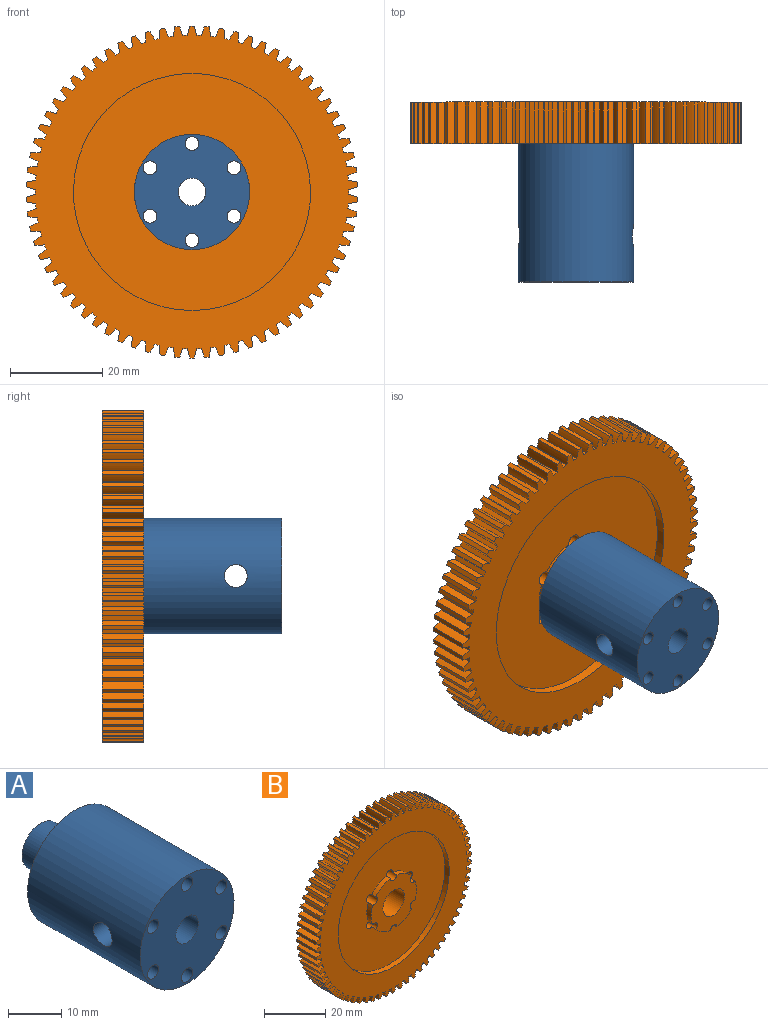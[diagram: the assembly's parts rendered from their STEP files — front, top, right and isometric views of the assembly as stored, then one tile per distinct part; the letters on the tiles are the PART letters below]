
ASSEMBLY  parts=2 mates=1
PART A: 14 faces, bbox 25x39x25 mm
  f0: cylinder r=3mm len=39mm, axis (0,1,0), area 691mm2, adj f2,f10,f11,f13
  f1: cylinder r=12.5mm len=30mm, axis (0,1,0), area 2316.8mm2, adj f2,f3,f10,f11
  f2: plane 25x25mm, normal (0,-1,0), area 420.2mm2, adj f0,f1,f4,f5,f6,f7,f8,f9
  f3: plane 25x25mm, normal (0,1,0), area 369.9mm2, adj f1,f4,f5,f6,f7,f8,f9,f12
  f4: cylinder r=1.5mm len=30mm, axis (0,1,0), area 282.7mm2, adj f2,f3
  f5: cylinder r=1.5mm len=30mm, axis (0,1,0), area 282.7mm2, adj f2,f3
  f6: cylinder r=1.5mm len=30mm, axis (0,1,0), area 282.7mm2, adj f2,f3
  f7: cylinder r=1.5mm len=30mm, axis (0,1,0), area 282.7mm2, adj f2,f3
  f8: cylinder r=1.5mm len=30mm, axis (0,1,0), area 282.7mm2, adj f2,f3
  f9: cylinder r=1.5mm len=30mm, axis (0,1,0), area 282.7mm2, adj f2,f3
  f10: cylinder r=2.5mm len=10.84mm, axis (-1,0,0), area 157mm2, adj f0,f1
  f11: cylinder r=2.5mm len=10.84mm, axis (-1,0,0), area 157mm2, adj f0,f1
  f12: cylinder r=5mm len=10mm, axis (0,-1,0), area 282.7mm2, adj f3,f13
  f13: plane 10x10mm, normal (0,1,0), area 50.3mm2, adj f0,f12
PART B: 307 faces, bbox 72x9x72 mm
  f0: cylinder r=10.5mm len=6.76mm, axis (0,1,0), area 16mm2, adj f296,f298,f305,f306
  f1: cylinder r=10.5mm len=6.76mm, axis (0,1,0), area 16mm2, adj f296,f298,f301,f306
  f2: cylinder r=10.5mm len=7.8mm, axis (0,1,0), area 16mm2, adj f296,f298,f304,f305
  f3: cylinder r=10.5mm len=6.76mm, axis (0,1,0), area 16mm2, adj f296,f298,f303,f304
  f4: cylinder r=10.5mm len=6.76mm, axis (0,1,0), area 16mm2, adj f296,f298,f302,f303
  f5: cylinder r=10.5mm len=7.8mm, axis (0,1,0), area 16mm2, adj f296,f298,f301,f302
  f6: cylinder r=10.5mm len=6.76mm, axis (0,1,0), area 16mm2, adj f12,f300,f305,f306
  f7: cylinder r=10.5mm len=6.76mm, axis (0,1,0), area 16mm2, adj f12,f300,f301,f306
  f8: cylinder r=10.5mm len=7.8mm, axis (0,1,0), area 16mm2, adj f12,f300,f304,f305
  f9: cylinder r=10.5mm len=6.76mm, axis (0,1,0), area 16mm2, adj f12,f300,f303,f304
  f10: cylinder r=10.5mm len=6.76mm, axis (0,1,0), area 16mm2, adj f12,f300,f302,f303
  f11: cylinder r=10.5mm len=7.8mm, axis (0,1,0), area 16mm2, adj f12,f300,f301,f302
  f12: plane 21x20.79mm, normal (0,1,0), area 247.3mm2, adj f6,f7,f8,f9,f10,f11,f297,f301
  f13: cylinder r=34mm len=9mm, axis (0,1,0), area 9.8mm2, adj f82,f87,f88,f193
  f14: cylinder r=34mm len=9mm, axis (0,1,0), area 9.8mm2, adj f87,f88,f190,f192
  f15: cylinder r=34mm len=9mm, axis (0,1,0), area 9.8mm2, adj f87,f88,f187,f189
  f16: cylinder r=34mm len=9mm, axis (0,1,0), area 9.8mm2, adj f87,f88,f184,f186
  f17: cylinder r=34mm len=9mm, axis (0,1,0), area 9.8mm2, adj f87,f88,f181,f183
  f18: cylinder r=34mm len=9mm, axis (0,1,0), area 9.8mm2, adj f87,f88,f178,f180
  f19: cylinder r=34mm len=9mm, axis (0,1,0), area 9.8mm2, adj f87,f88,f175,f177
  f20: cylinder r=34mm len=9mm, axis (0,1,0), area 9.8mm2, adj f87,f88,f172,f174
  f21: cylinder r=34mm len=9mm, axis (0,1,0), area 9.8mm2, adj f87,f88,f169,f171
  f22: cylinder r=34mm len=9mm, axis (0,1,0), area 9.8mm2, adj f87,f88,f166,f168
  f23: cylinder r=34mm len=9mm, axis (0,1,0), area 9.8mm2, adj f87,f88,f163,f165
  f24: cylinder r=34mm len=9mm, axis (0,1,0), area 9.8mm2, adj f87,f88,f160,f162
  f25: cylinder r=34mm len=9mm, axis (0,1,0), area 9.8mm2, adj f87,f88,f157,f159
  f26: cylinder r=34mm len=9mm, axis (0,1,0), area 9.8mm2, adj f87,f88,f154,f156
  f27: cylinder r=34mm len=9mm, axis (0,1,0), area 9.8mm2, adj f87,f88,f151,f153
  f28: cylinder r=34mm len=9mm, axis (0,1,0), area 9.8mm2, adj f87,f88,f148,f150
  f29: cylinder r=34mm len=9mm, axis (0,1,0), area 9.8mm2, adj f87,f88,f145,f147
  f30: cylinder r=34mm len=9mm, axis (0,1,0), area 9.8mm2, adj f87,f88,f142,f144
  f31: cylinder r=34mm len=9mm, axis (0,1,0), area 9.8mm2, adj f87,f88,f139,f141
  f32: cylinder r=34mm len=9mm, axis (0,1,0), area 9.8mm2, adj f87,f88,f136,f138
  f33: cylinder r=34mm len=9mm, axis (0,1,0), area 9.8mm2, adj f87,f88,f133,f135
  f34: cylinder r=34mm len=9mm, axis (0,1,0), area 9.8mm2, adj f87,f88,f130,f132
  f35: cylinder r=34mm len=9mm, axis (0,1,0), area 9.8mm2, adj f87,f88,f127,f129
  f36: cylinder r=34mm len=9mm, axis (0,1,0), area 9.8mm2, adj f87,f88,f124,f126
  f37: cylinder r=34mm len=9mm, axis (0,1,0), area 9.8mm2, adj f87,f88,f121,f123
  f38: cylinder r=34mm len=9mm, axis (0,1,0), area 9.8mm2, adj f87,f88,f118,f120
  f39: cylinder r=34mm len=9mm, axis (0,1,0), area 9.8mm2, adj f87,f88,f115,f117
  f40: cylinder r=34mm len=9mm, axis (0,1,0), area 9.8mm2, adj f87,f88,f112,f114
  f41: cylinder r=34mm len=9mm, axis (0,1,0), area 9.8mm2, adj f87,f88,f109,f111
  f42: cylinder r=34mm len=9mm, axis (0,1,0), area 9.8mm2, adj f87,f88,f106,f108
  f43: cylinder r=34mm len=9mm, axis (0,1,0), area 9.8mm2, adj f87,f88,f103,f105
  f44: cylinder r=34mm len=9mm, axis (0,1,0), area 9.8mm2, adj f87,f88,f100,f102
  f45: cylinder r=34mm len=9mm, axis (0,1,0), area 9.8mm2, adj f87,f88,f97,f99
  f46: cylinder r=34mm len=9mm, axis (0,1,0), area 9.8mm2, adj f87,f88,f94,f96
  f47: cylinder r=34mm len=9mm, axis (0,1,0), area 9.8mm2, adj f87,f88,f91,f93
  f48: cylinder r=34mm len=9mm, axis (0,1,0), area 9.8mm2, adj f87,f88,f90,f294
  f49: cylinder r=34mm len=9mm, axis (0,1,0), area 9.8mm2, adj f87,f88,f292,f293
  f50: cylinder r=34mm len=9mm, axis (0,1,0), area 9.8mm2, adj f87,f88,f289,f291
  f51: cylinder r=34mm len=9mm, axis (0,1,0), area 9.8mm2, adj f87,f88,f286,f288
  f52: cylinder r=34mm len=9mm, axis (0,1,0), area 9.8mm2, adj f87,f88,f283,f285
  f53: cylinder r=34mm len=9mm, axis (0,1,0), area 9.8mm2, adj f87,f88,f280,f282
  f54: cylinder r=34mm len=9mm, axis (0,1,0), area 9.8mm2, adj f87,f88,f277,f279
  f55: cylinder r=34mm len=9mm, axis (0,1,0), area 9.8mm2, adj f87,f88,f274,f276
  f56: cylinder r=34mm len=9mm, axis (0,1,0), area 9.8mm2, adj f87,f88,f271,f273
  f57: cylinder r=34mm len=9mm, axis (0,1,0), area 9.8mm2, adj f87,f88,f268,f270
  f58: cylinder r=34mm len=9mm, axis (0,1,0), area 9.8mm2, adj f87,f88,f265,f267
  f59: cylinder r=34mm len=9mm, axis (0,1,0), area 9.8mm2, adj f87,f88,f262,f264
  f60: cylinder r=34mm len=9mm, axis (0,1,0), area 9.8mm2, adj f87,f88,f259,f261
  f61: cylinder r=34mm len=9mm, axis (0,1,0), area 9.8mm2, adj f87,f88,f256,f258
  f62: cylinder r=34mm len=9mm, axis (0,1,0), area 9.8mm2, adj f87,f88,f253,f255
  f63: cylinder r=34mm len=9mm, axis (0,1,0), area 9.8mm2, adj f87,f88,f250,f252
  f64: cylinder r=34mm len=9mm, axis (0,1,0), area 9.8mm2, adj f87,f88,f247,f249
  f65: cylinder r=34mm len=9mm, axis (0,1,0), area 9.8mm2, adj f87,f88,f244,f246
  f66: cylinder r=34mm len=9mm, axis (0,1,0), area 9.8mm2, adj f87,f88,f241,f243
  f67: cylinder r=34mm len=9mm, axis (0,1,0), area 9.8mm2, adj f87,f88,f238,f240
  f68: cylinder r=34mm len=9mm, axis (0,1,0), area 9.8mm2, adj f87,f88,f235,f237
  f69: cylinder r=34mm len=9mm, axis (0,1,0), area 9.8mm2, adj f87,f88,f232,f234
  f70: cylinder r=34mm len=9mm, axis (0,1,0), area 9.8mm2, adj f87,f88,f229,f231
  f71: cylinder r=34mm len=9mm, axis (0,1,0), area 9.8mm2, adj f87,f88,f226,f228
  f72: cylinder r=34mm len=9mm, axis (0,1,0), area 9.8mm2, adj f87,f88,f223,f225
  f73: cylinder r=34mm len=9mm, axis (0,1,0), area 9.8mm2, adj f87,f88,f220,f222
  f74: cylinder r=34mm len=9mm, axis (0,1,0), area 9.8mm2, adj f87,f88,f217,f219
  f75: cylinder r=34mm len=9mm, axis (0,1,0), area 9.8mm2, adj f87,f88,f214,f216
  f76: cylinder r=34mm len=9mm, axis (0,1,0), area 9.8mm2, adj f87,f88,f211,f213
  f77: cylinder r=34mm len=9mm, axis (0,1,0), area 9.8mm2, adj f87,f88,f208,f210
  f78: cylinder r=34mm len=9mm, axis (0,1,0), area 9.8mm2, adj f87,f88,f205,f207
  f79: cylinder r=34mm len=9mm, axis (0,1,0), area 9.8mm2, adj f87,f88,f202,f204
  f80: cylinder r=34mm len=9mm, axis (0,1,0), area 9.8mm2, adj f87,f88,f199,f201
  f81: cylinder r=34mm len=9mm, axis (0,1,0), area 9.8mm2, adj f87,f88,f195,f198
  f82: cylinder r=11.84mm len=9mm, axis (0,1,0), area 18.7mm2, adj f13,f85,f87,f88
  f83: cylinder r=34mm len=9mm, axis (0,1,0), area 9.8mm2, adj f84,f87,f88,f196
  f84: cylinder r=11.84mm len=9mm, axis (0,1,0), area 18.7mm2, adj f83,f85,f87,f88
  f85: plane 9x1mm, normal (0,0,1), area 9mm2, adj f82,f84,f87,f88
  f86: cylinder r=25.7mm len=51.4mm, axis (0,1,0), area 323mm2, adj f87,f296
  f87: plane 72x71.97mm, normal (0,-1,0), area 1772.8mm2, adj f13,f14,f15,f16,f17,f18,f19,f20
  f88: plane 72x71.97mm, normal (0,1,0), area 1772.8mm2, adj f13,f14,f15,f16,f17,f18,f19,f20
  f89: plane 9x1mm, normal (0,0,-1), area 9mm2, adj f87,f88,f90,f91
  f90: cylinder r=11.84mm len=9mm, axis (0,1,0), area 18.7mm2, adj f48,f87,f88,f89
  f91: cylinder r=11.84mm len=9mm, axis (0,1,0), area 18.7mm2, adj f47,f87,f88,f89
  f92: plane 9x1mm, normal (-0.09,0,-1), area 9mm2, adj f87,f88,f93,f94
  f93: cylinder r=11.84mm len=9mm, axis (0,1,0), area 18.7mm2, adj f47,f87,f88,f92
  f94: cylinder r=11.84mm len=9mm, axis (0,1,0), area 18.7mm2, adj f46,f87,f88,f92
  f95: plane 9x0.98mm, normal (-0.18,0,-0.98), area 9mm2, adj f87,f88,f96,f97
  f96: cylinder r=11.84mm len=9mm, axis (0,1,0), area 18.7mm2, adj f46,f87,f88,f95
  f97: cylinder r=11.84mm len=9mm, axis (0,1,0), area 18.7mm2, adj f45,f87,f88,f95
  f98: plane 9x0.96mm, normal (-0.27,0,-0.96), area 9mm2, adj f87,f88,f99,f100
  f99: cylinder r=11.84mm len=9mm, axis (0,1,0), area 18.7mm2, adj f45,f87,f88,f98
  f100: cylinder r=11.84mm len=9mm, axis (0,1,0), area 18.7mm2, adj f44,f87,f88,f98
  f101: plane 9x0.94mm, normal (-0.35,0,-0.94), area 9mm2, adj f87,f88,f102,f103
  f102: cylinder r=11.84mm len=9mm, axis (0,1,0), area 18.7mm2, adj f44,f87,f88,f101
  f103: cylinder r=11.84mm len=9mm, axis (0,1,0), area 18.7mm2, adj f43,f87,f88,f101
  f104: plane 9x0.9mm, normal (-0.43,0,-0.9), area 9mm2, adj f87,f88,f105,f106
  f105: cylinder r=11.84mm len=9mm, axis (0,1,0), area 18.7mm2, adj f43,f87,f88,f104
  f106: cylinder r=11.84mm len=9mm, axis (0,1,0), area 18.7mm2, adj f42,f87,f88,f104
  f107: plane 9x0.86mm, normal (-0.51,0,-0.86), area 9mm2, adj f87,f88,f108,f109
  f108: cylinder r=11.84mm len=9mm, axis (0,1,0), area 18.7mm2, adj f42,f87,f88,f107
  f109: cylinder r=11.84mm len=9mm, axis (0,1,0), area 18.7mm2, adj f41,f87,f88,f107
  f110: plane 9x0.81mm, normal (-0.59,0,-0.81), area 9mm2, adj f87,f88,f111,f112
  f111: cylinder r=11.84mm len=9mm, axis (0,1,0), area 18.7mm2, adj f41,f87,f88,f110
  f112: cylinder r=11.84mm len=9mm, axis (0,1,0), area 18.7mm2, adj f40,f87,f88,f110
  f113: plane 9x0.75mm, normal (-0.66,0,-0.75), area 9mm2, adj f87,f88,f114,f115
  f114: cylinder r=11.84mm len=9mm, axis (0,1,0), area 18.7mm2, adj f40,f87,f88,f113
  f115: cylinder r=11.84mm len=9mm, axis (0,1,0), area 18.7mm2, adj f39,f87,f88,f113
  f116: plane 9x0.72mm, normal (-0.72,0,-0.69), area 9mm2, adj f87,f88,f117,f118
  f117: cylinder r=11.84mm len=9mm, axis (0,1,0), area 18.7mm2, adj f39,f87,f88,f116
  f118: cylinder r=11.84mm len=9mm, axis (0,1,0), area 18.7mm2, adj f38,f87,f88,f116
  f119: plane 9x0.78mm, normal (-0.78,0,-0.62), area 9mm2, adj f87,f88,f120,f121
  f120: cylinder r=11.84mm len=9mm, axis (0,1,0), area 18.7mm2, adj f38,f87,f88,f119
  f121: cylinder r=11.84mm len=9mm, axis (0,1,0), area 18.7mm2, adj f37,f87,f88,f119
  f122: plane 9x0.83mm, normal (-0.83,0,-0.55), area 9mm2, adj f87,f88,f123,f124
  f123: cylinder r=11.84mm len=9mm, axis (0,1,0), area 18.7mm2, adj f37,f87,f88,f122
  f124: cylinder r=11.84mm len=9mm, axis (0,1,0), area 18.7mm2, adj f36,f87,f88,f122
  f125: plane 9x0.88mm, normal (-0.88,0,-0.47), area 9mm2, adj f87,f88,f126,f127
  f126: cylinder r=11.84mm len=9mm, axis (0,1,0), area 18.7mm2, adj f36,f87,f88,f125
  f127: cylinder r=11.84mm len=9mm, axis (0,1,0), area 18.7mm2, adj f35,f87,f88,f125
  f128: plane 9x0.92mm, normal (-0.92,0,-0.39), area 9mm2, adj f87,f88,f129,f130
  f129: cylinder r=11.84mm len=9mm, axis (0,1,0), area 18.7mm2, adj f35,f87,f88,f128
  f130: cylinder r=11.84mm len=9mm, axis (0,1,0), area 18.7mm2, adj f34,f87,f88,f128
  f131: plane 9x0.95mm, normal (-0.95,0,-0.31), area 9mm2, adj f87,f88,f132,f133
  f132: cylinder r=11.84mm len=9mm, axis (0,1,0), area 18.7mm2, adj f34,f87,f88,f131
  f133: cylinder r=11.84mm len=9mm, axis (0,1,0), area 18.7mm2, adj f33,f87,f88,f131
  f134: plane 9x0.98mm, normal (-0.97,0,-0.22), area 9mm2, adj f87,f88,f135,f136
  f135: cylinder r=11.84mm len=9mm, axis (0,1,0), area 18.7mm2, adj f33,f87,f88,f134
  f136: cylinder r=11.84mm len=9mm, axis (0,1,0), area 18.7mm2, adj f32,f87,f88,f134
  f137: plane 9x0.99mm, normal (-0.99,0,-0.13), area 9mm2, adj f87,f88,f138,f139
  f138: cylinder r=11.84mm len=9mm, axis (0,1,0), area 18.7mm2, adj f32,f87,f88,f137
  f139: cylinder r=11.84mm len=9mm, axis (0,1,0), area 18.7mm2, adj f31,f87,f88,f137
  f140: plane 9x1mm, normal (-1,0,-0.04), area 9mm2, adj f87,f88,f141,f142
  f141: cylinder r=11.84mm len=9mm, axis (0,1,0), area 18.7mm2, adj f31,f87,f88,f140
  f142: cylinder r=11.84mm len=9mm, axis (0,1,0), area 18.7mm2, adj f30,f87,f88,f140
  f143: plane 9x1mm, normal (-1,0,0.04), area 9mm2, adj f87,f88,f144,f145
  f144: cylinder r=11.84mm len=9mm, axis (0,1,0), area 18.7mm2, adj f30,f87,f88,f143
  f145: cylinder r=11.84mm len=9mm, axis (0,1,0), area 18.7mm2, adj f29,f87,f88,f143
  f146: plane 9x0.99mm, normal (-0.99,0,0.13), area 9mm2, adj f87,f88,f147,f148
  f147: cylinder r=11.84mm len=9mm, axis (0,1,0), area 18.7mm2, adj f29,f87,f88,f146
  f148: cylinder r=11.84mm len=9mm, axis (0,1,0), area 18.7mm2, adj f28,f87,f88,f146
  f149: plane 9x0.98mm, normal (-0.97,0,0.22), area 9mm2, adj f87,f88,f150,f151
  f150: cylinder r=11.84mm len=9mm, axis (0,1,0), area 18.7mm2, adj f28,f87,f88,f149
  f151: cylinder r=11.84mm len=9mm, axis (0,1,0), area 18.7mm2, adj f27,f87,f88,f149
  f152: plane 9x0.95mm, normal (-0.95,0,0.31), area 9mm2, adj f87,f88,f153,f154
  f153: cylinder r=11.84mm len=9mm, axis (0,1,0), area 18.7mm2, adj f27,f87,f88,f152
  f154: cylinder r=11.84mm len=9mm, axis (0,1,0), area 18.7mm2, adj f26,f87,f88,f152
  f155: plane 9x0.92mm, normal (-0.92,0,0.39), area 9mm2, adj f87,f88,f156,f157
  f156: cylinder r=11.84mm len=9mm, axis (0,1,0), area 18.7mm2, adj f26,f87,f88,f155
  f157: cylinder r=11.84mm len=9mm, axis (0,1,0), area 18.7mm2, adj f25,f87,f88,f155
  f158: plane 9x0.88mm, normal (-0.88,0,0.47), area 9mm2, adj f87,f88,f159,f160
  f159: cylinder r=11.84mm len=9mm, axis (0,1,0), area 18.7mm2, adj f25,f87,f88,f158
  f160: cylinder r=11.84mm len=9mm, axis (0,1,0), area 18.7mm2, adj f24,f87,f88,f158
  f161: plane 9x0.83mm, normal (-0.83,0,0.55), area 9mm2, adj f87,f88,f162,f163
  f162: cylinder r=11.84mm len=9mm, axis (0,1,0), area 18.7mm2, adj f24,f87,f88,f161
  f163: cylinder r=11.84mm len=9mm, axis (0,1,0), area 18.7mm2, adj f23,f87,f88,f161
  f164: plane 9x0.78mm, normal (-0.78,0,0.62), area 9mm2, adj f87,f88,f165,f166
  f165: cylinder r=11.84mm len=9mm, axis (0,1,0), area 18.7mm2, adj f23,f87,f88,f164
  f166: cylinder r=11.84mm len=9mm, axis (0,1,0), area 18.7mm2, adj f22,f87,f88,f164
  f167: plane 9x0.72mm, normal (-0.72,0,0.69), area 9mm2, adj f87,f88,f168,f169
  f168: cylinder r=11.84mm len=9mm, axis (0,1,0), area 18.7mm2, adj f22,f87,f88,f167
  f169: cylinder r=11.84mm len=9mm, axis (0,1,0), area 18.7mm2, adj f21,f87,f88,f167
  f170: plane 9x0.75mm, normal (-0.66,0,0.75), area 9mm2, adj f87,f88,f171,f172
  f171: cylinder r=11.84mm len=9mm, axis (0,1,0), area 18.7mm2, adj f21,f87,f88,f170
  f172: cylinder r=11.84mm len=9mm, axis (0,1,0), area 18.7mm2, adj f20,f87,f88,f170
  f173: plane 9x0.81mm, normal (-0.59,0,0.81), area 9mm2, adj f87,f88,f174,f175
  f174: cylinder r=11.84mm len=9mm, axis (0,1,0), area 18.7mm2, adj f20,f87,f88,f173
  f175: cylinder r=11.84mm len=9mm, axis (0,1,0), area 18.7mm2, adj f19,f87,f88,f173
  f176: plane 9x0.86mm, normal (-0.51,0,0.86), area 9mm2, adj f87,f88,f177,f178
  f177: cylinder r=11.84mm len=9mm, axis (0,1,0), area 18.7mm2, adj f19,f87,f88,f176
  f178: cylinder r=11.84mm len=9mm, axis (0,1,0), area 18.7mm2, adj f18,f87,f88,f176
  f179: plane 9x0.9mm, normal (-0.43,0,0.9), area 9mm2, adj f87,f88,f180,f181
  f180: cylinder r=11.84mm len=9mm, axis (0,1,0), area 18.7mm2, adj f18,f87,f88,f179
  f181: cylinder r=11.84mm len=9mm, axis (0,1,0), area 18.7mm2, adj f17,f87,f88,f179
  f182: plane 9x0.94mm, normal (-0.35,0,0.94), area 9mm2, adj f87,f88,f183,f184
  f183: cylinder r=11.84mm len=9mm, axis (0,1,0), area 18.7mm2, adj f17,f87,f88,f182
  f184: cylinder r=11.84mm len=9mm, axis (0,1,0), area 18.7mm2, adj f16,f87,f88,f182
  f185: plane 9x0.96mm, normal (-0.27,0,0.96), area 9mm2, adj f87,f88,f186,f187
  f186: cylinder r=11.84mm len=9mm, axis (0,1,0), area 18.7mm2, adj f16,f87,f88,f185
  f187: cylinder r=11.84mm len=9mm, axis (0,1,0), area 18.7mm2, adj f15,f87,f88,f185
  f188: plane 9x0.98mm, normal (-0.18,0,0.98), area 9mm2, adj f87,f88,f189,f190
  f189: cylinder r=11.84mm len=9mm, axis (0,1,0), area 18.7mm2, adj f15,f87,f88,f188
  f190: cylinder r=11.84mm len=9mm, axis (0,1,0), area 18.7mm2, adj f14,f87,f88,f188
  f191: plane 9x1mm, normal (-0.09,0,1), area 9mm2, adj f87,f88,f192,f193
  f192: cylinder r=11.84mm len=9mm, axis (0,1,0), area 18.7mm2, adj f14,f87,f88,f191
  f193: cylinder r=11.84mm len=9mm, axis (0,1,0), area 18.7mm2, adj f13,f87,f88,f191
  f194: plane 9x1mm, normal (0.09,0,1), area 9mm2, adj f87,f88,f195,f196
  f195: cylinder r=11.84mm len=9mm, axis (0,1,0), area 18.7mm2, adj f81,f87,f88,f194
  f196: cylinder r=11.84mm len=9mm, axis (0,1,0), area 18.7mm2, adj f83,f87,f88,f194
  f197: plane 9x0.98mm, normal (0.18,0,0.98), area 9mm2, adj f87,f88,f198,f199
  f198: cylinder r=11.84mm len=9mm, axis (0,1,0), area 18.7mm2, adj f81,f87,f88,f197
  f199: cylinder r=11.84mm len=9mm, axis (0,1,0), area 18.7mm2, adj f80,f87,f88,f197
  f200: plane 9x0.96mm, normal (0.27,0,0.96), area 9mm2, adj f87,f88,f201,f202
  f201: cylinder r=11.84mm len=9mm, axis (0,1,0), area 18.7mm2, adj f80,f87,f88,f200
  f202: cylinder r=11.84mm len=9mm, axis (0,1,0), area 18.7mm2, adj f79,f87,f88,f200
  f203: plane 9x0.94mm, normal (0.35,0,0.94), area 9mm2, adj f87,f88,f204,f205
  f204: cylinder r=11.84mm len=9mm, axis (0,1,0), area 18.7mm2, adj f79,f87,f88,f203
  f205: cylinder r=11.84mm len=9mm, axis (0,1,0), area 18.7mm2, adj f78,f87,f88,f203
  f206: plane 9x0.9mm, normal (0.43,0,0.9), area 9mm2, adj f87,f88,f207,f208
  f207: cylinder r=11.84mm len=9mm, axis (0,1,0), area 18.7mm2, adj f78,f87,f88,f206
  f208: cylinder r=11.84mm len=9mm, axis (0,1,0), area 18.7mm2, adj f77,f87,f88,f206
  f209: plane 9x0.86mm, normal (0.51,0,0.86), area 9mm2, adj f87,f88,f210,f211
  f210: cylinder r=11.84mm len=9mm, axis (0,1,0), area 18.7mm2, adj f77,f87,f88,f209
  f211: cylinder r=11.84mm len=9mm, axis (0,1,0), area 18.7mm2, adj f76,f87,f88,f209
  f212: plane 9x0.81mm, normal (0.59,0,0.81), area 9mm2, adj f87,f88,f213,f214
  f213: cylinder r=11.84mm len=9mm, axis (0,1,0), area 18.7mm2, adj f76,f87,f88,f212
  f214: cylinder r=11.84mm len=9mm, axis (0,1,0), area 18.7mm2, adj f75,f87,f88,f212
  f215: plane 9x0.75mm, normal (0.66,0,0.75), area 9mm2, adj f87,f88,f216,f217
  f216: cylinder r=11.84mm len=9mm, axis (0,1,0), area 18.7mm2, adj f75,f87,f88,f215
  f217: cylinder r=11.84mm len=9mm, axis (0,1,0), area 18.7mm2, adj f74,f87,f88,f215
  f218: plane 9x0.72mm, normal (0.72,0,0.69), area 9mm2, adj f87,f88,f219,f220
  f219: cylinder r=11.84mm len=9mm, axis (0,1,0), area 18.7mm2, adj f74,f87,f88,f218
  f220: cylinder r=11.84mm len=9mm, axis (0,1,0), area 18.7mm2, adj f73,f87,f88,f218
  f221: plane 9x0.78mm, normal (0.78,0,0.62), area 9mm2, adj f87,f88,f222,f223
  f222: cylinder r=11.84mm len=9mm, axis (0,1,0), area 18.7mm2, adj f73,f87,f88,f221
  f223: cylinder r=11.84mm len=9mm, axis (0,1,0), area 18.7mm2, adj f72,f87,f88,f221
  f224: plane 9x0.83mm, normal (0.83,0,0.55), area 9mm2, adj f87,f88,f225,f226
  f225: cylinder r=11.84mm len=9mm, axis (0,1,0), area 18.7mm2, adj f72,f87,f88,f224
  f226: cylinder r=11.84mm len=9mm, axis (0,1,0), area 18.7mm2, adj f71,f87,f88,f224
  f227: plane 9x0.88mm, normal (0.88,0,0.47), area 9mm2, adj f87,f88,f228,f229
  f228: cylinder r=11.84mm len=9mm, axis (0,1,0), area 18.7mm2, adj f71,f87,f88,f227
  f229: cylinder r=11.84mm len=9mm, axis (0,1,0), area 18.7mm2, adj f70,f87,f88,f227
  f230: plane 9x0.92mm, normal (0.92,0,0.39), area 9mm2, adj f87,f88,f231,f232
  f231: cylinder r=11.84mm len=9mm, axis (0,1,0), area 18.7mm2, adj f70,f87,f88,f230
  f232: cylinder r=11.84mm len=9mm, axis (0,1,0), area 18.7mm2, adj f69,f87,f88,f230
  f233: plane 9x0.95mm, normal (0.95,0,0.31), area 9mm2, adj f87,f88,f234,f235
  f234: cylinder r=11.84mm len=9mm, axis (0,1,0), area 18.7mm2, adj f69,f87,f88,f233
  f235: cylinder r=11.84mm len=9mm, axis (0,1,0), area 18.7mm2, adj f68,f87,f88,f233
  f236: plane 9x0.98mm, normal (0.97,0,0.22), area 9mm2, adj f87,f88,f237,f238
  f237: cylinder r=11.84mm len=9mm, axis (0,1,0), area 18.7mm2, adj f68,f87,f88,f236
  f238: cylinder r=11.84mm len=9mm, axis (0,1,0), area 18.7mm2, adj f67,f87,f88,f236
  f239: plane 9x0.99mm, normal (0.99,0,0.13), area 9mm2, adj f87,f88,f240,f241
  f240: cylinder r=11.84mm len=9mm, axis (0,1,0), area 18.7mm2, adj f67,f87,f88,f239
  f241: cylinder r=11.84mm len=9mm, axis (0,1,0), area 18.7mm2, adj f66,f87,f88,f239
  f242: plane 9x1mm, normal (1,0,0.04), area 9mm2, adj f87,f88,f243,f244
  f243: cylinder r=11.84mm len=9mm, axis (0,1,0), area 18.7mm2, adj f66,f87,f88,f242
  f244: cylinder r=11.84mm len=9mm, axis (0,1,0), area 18.7mm2, adj f65,f87,f88,f242
  f245: plane 9x1mm, normal (1,0,-0.04), area 9mm2, adj f87,f88,f246,f247
  f246: cylinder r=11.84mm len=9mm, axis (0,1,0), area 18.7mm2, adj f65,f87,f88,f245
  f247: cylinder r=11.84mm len=9mm, axis (0,1,0), area 18.7mm2, adj f64,f87,f88,f245
  f248: plane 9x0.99mm, normal (0.99,0,-0.13), area 9mm2, adj f87,f88,f249,f250
  f249: cylinder r=11.84mm len=9mm, axis (0,1,0), area 18.7mm2, adj f64,f87,f88,f248
  f250: cylinder r=11.84mm len=9mm, axis (0,1,0), area 18.7mm2, adj f63,f87,f88,f248
  f251: plane 9x0.98mm, normal (0.97,0,-0.22), area 9mm2, adj f87,f88,f252,f253
  f252: cylinder r=11.84mm len=9mm, axis (0,1,0), area 18.7mm2, adj f63,f87,f88,f251
  f253: cylinder r=11.84mm len=9mm, axis (0,1,0), area 18.7mm2, adj f62,f87,f88,f251
  f254: plane 9x0.95mm, normal (0.95,0,-0.31), area 9mm2, adj f87,f88,f255,f256
  f255: cylinder r=11.84mm len=9mm, axis (0,1,0), area 18.7mm2, adj f62,f87,f88,f254
  f256: cylinder r=11.84mm len=9mm, axis (0,1,0), area 18.7mm2, adj f61,f87,f88,f254
  f257: plane 9x0.92mm, normal (0.92,0,-0.39), area 9mm2, adj f87,f88,f258,f259
  f258: cylinder r=11.84mm len=9mm, axis (0,1,0), area 18.7mm2, adj f61,f87,f88,f257
  f259: cylinder r=11.84mm len=9mm, axis (0,1,0), area 18.7mm2, adj f60,f87,f88,f257
  f260: plane 9x0.88mm, normal (0.88,0,-0.47), area 9mm2, adj f87,f88,f261,f262
  f261: cylinder r=11.84mm len=9mm, axis (0,1,0), area 18.7mm2, adj f60,f87,f88,f260
  f262: cylinder r=11.84mm len=9mm, axis (0,1,0), area 18.7mm2, adj f59,f87,f88,f260
  f263: plane 9x0.83mm, normal (0.83,0,-0.55), area 9mm2, adj f87,f88,f264,f265
  f264: cylinder r=11.84mm len=9mm, axis (0,1,0), area 18.7mm2, adj f59,f87,f88,f263
  f265: cylinder r=11.84mm len=9mm, axis (0,1,0), area 18.7mm2, adj f58,f87,f88,f263
  f266: plane 9x0.78mm, normal (0.78,0,-0.62), area 9mm2, adj f87,f88,f267,f268
  f267: cylinder r=11.84mm len=9mm, axis (0,1,0), area 18.7mm2, adj f58,f87,f88,f266
  f268: cylinder r=11.84mm len=9mm, axis (0,1,0), area 18.7mm2, adj f57,f87,f88,f266
  f269: plane 9x0.72mm, normal (0.72,0,-0.69), area 9mm2, adj f87,f88,f270,f271
  f270: cylinder r=11.84mm len=9mm, axis (0,1,0), area 18.7mm2, adj f57,f87,f88,f269
  f271: cylinder r=11.84mm len=9mm, axis (0,1,0), area 18.7mm2, adj f56,f87,f88,f269
  f272: plane 9x0.75mm, normal (0.66,0,-0.75), area 9mm2, adj f87,f88,f273,f274
  f273: cylinder r=11.84mm len=9mm, axis (0,1,0), area 18.7mm2, adj f56,f87,f88,f272
  f274: cylinder r=11.84mm len=9mm, axis (0,1,0), area 18.7mm2, adj f55,f87,f88,f272
  f275: plane 9x0.81mm, normal (0.59,0,-0.81), area 9mm2, adj f87,f88,f276,f277
  f276: cylinder r=11.84mm len=9mm, axis (0,1,0), area 18.7mm2, adj f55,f87,f88,f275
  f277: cylinder r=11.84mm len=9mm, axis (0,1,0), area 18.7mm2, adj f54,f87,f88,f275
  f278: plane 9x0.86mm, normal (0.51,0,-0.86), area 9mm2, adj f87,f88,f279,f280
  f279: cylinder r=11.84mm len=9mm, axis (0,1,0), area 18.7mm2, adj f54,f87,f88,f278
  f280: cylinder r=11.84mm len=9mm, axis (0,1,0), area 18.7mm2, adj f53,f87,f88,f278
  f281: plane 9x0.9mm, normal (0.43,0,-0.9), area 9mm2, adj f87,f88,f282,f283
  f282: cylinder r=11.84mm len=9mm, axis (0,1,0), area 18.7mm2, adj f53,f87,f88,f281
  f283: cylinder r=11.84mm len=9mm, axis (0,1,0), area 18.7mm2, adj f52,f87,f88,f281
  f284: plane 9x0.94mm, normal (0.35,0,-0.94), area 9mm2, adj f87,f88,f285,f286
  f285: cylinder r=11.84mm len=9mm, axis (0,1,0), area 18.7mm2, adj f52,f87,f88,f284
  f286: cylinder r=11.84mm len=9mm, axis (0,1,0), area 18.7mm2, adj f51,f87,f88,f284
  f287: plane 9x0.96mm, normal (0.27,0,-0.96), area 9mm2, adj f87,f88,f288,f289
  f288: cylinder r=11.84mm len=9mm, axis (0,1,0), area 18.7mm2, adj f51,f87,f88,f287
  f289: cylinder r=11.84mm len=9mm, axis (0,1,0), area 18.7mm2, adj f50,f87,f88,f287
  f290: plane 9x0.98mm, normal (0.18,0,-0.98), area 9mm2, adj f87,f88,f291,f292
  f291: cylinder r=11.84mm len=9mm, axis (0,1,0), area 18.7mm2, adj f50,f87,f88,f290
  f292: cylinder r=11.84mm len=9mm, axis (0,1,0), area 18.7mm2, adj f49,f87,f88,f290
  f293: cylinder r=11.84mm len=9mm, axis (0,1,0), area 18.7mm2, adj f49,f87,f88,f295
  f294: cylinder r=11.84mm len=9mm, axis (0,1,0), area 18.7mm2, adj f48,f87,f88,f295
  f295: plane 9x1mm, normal (0.09,0,-1), area 9mm2, adj f87,f88,f293,f294
  f296: plane 51.4x51.4mm, normal (0,-1,0), area 1706.8mm2, adj f0,f1,f2,f3,f4,f5,f86,f301
  f297: cylinder r=5mm len=10mm, axis (0,1,0), area 282.7mm2, adj f12,f298
  f298: plane 21x20.79mm, normal (0,-1,0), area 247.3mm2, adj f0,f1,f2,f3,f4,f5,f297,f301
  f299: cylinder r=25.7mm len=51.4mm, axis (0,1,0), area 323mm2, adj f88,f300
  f300: plane 51.4x51.4mm, normal (0,1,0), area 1706.8mm2, adj f6,f7,f8,f9,f10,f11,f299,f301
  f301: cylinder r=1.5mm len=9mm, axis (0,1,0), area 65.1mm2, adj f1,f5,f7,f11,f12,f296,f298,f300
  f302: cylinder r=1.5mm len=9mm, axis (0,1,0), area 65.1mm2, adj f4,f5,f10,f11,f12,f296,f298,f300
  f303: cylinder r=1.5mm len=9mm, axis (0,1,0), area 65.1mm2, adj f3,f4,f9,f10,f12,f296,f298,f300
  f304: cylinder r=1.5mm len=9mm, axis (0,1,0), area 65.1mm2, adj f2,f3,f8,f9,f12,f296,f298,f300
  f305: cylinder r=1.5mm len=9mm, axis (0,1,0), area 65.1mm2, adj f0,f2,f6,f8,f12,f296,f298,f300
  f306: cylinder r=1.5mm len=9mm, axis (0,1,0), area 65.1mm2, adj f0,f1,f6,f7,f12,f296,f298,f300
PLACE A t=(-33.33,-14.08,0.24)mm
PLACE B t=(-33.33,-5.08,0.24)mm
MATE fastened A.f1 <-> B.f0  axis (0,1,0) through (-33.33,-14.08,0.24)mm
